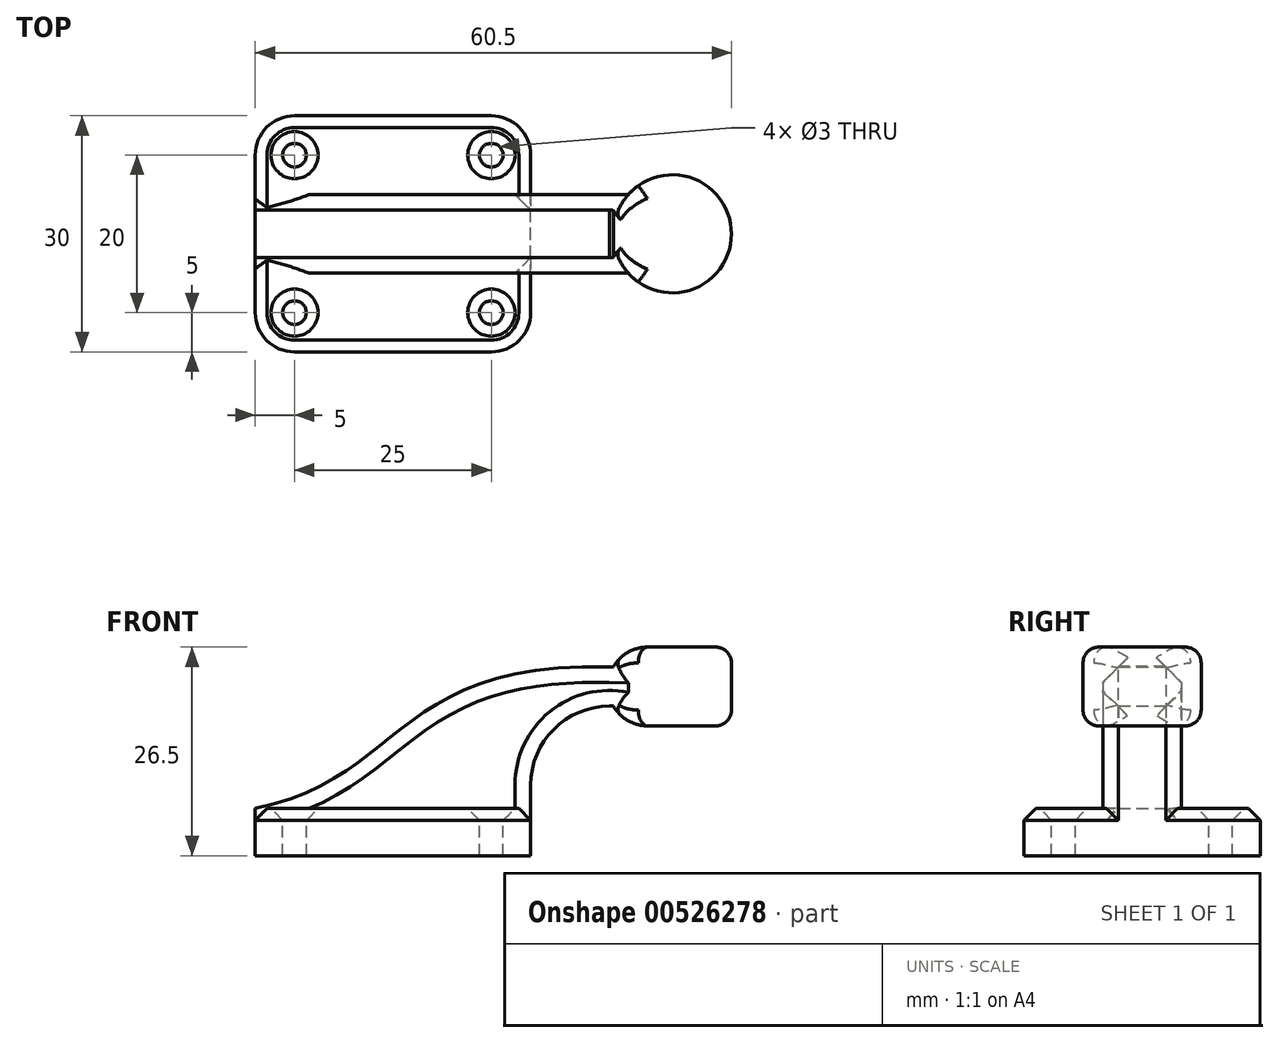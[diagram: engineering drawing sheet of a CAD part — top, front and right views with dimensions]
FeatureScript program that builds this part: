
annotation { "Feature Type Name" : "Feature", "Feature Type Description" : "" }
export const myFeature = defineFeature(function(context is Context, id is Id, definition is map)
    precondition{}
    {
        {
            var Q0;
            Q0=qCreatedBy(makeId("Front.planeOp"),FACE);
            var sketch = newSketch(context, id + "F0", { "sketchPlane" : qUnion([Q0])});
            skLineSegment(sketch, "E0.bottom", {"start": v(17.5, -3) * mm, "end": v(-17.5, -3) * mm});
            skLineSegment(sketch, "E0.top", {"start": v(17.5, 3) * mm, "end": v(-17.5, 3) * mm});
            skLineSegment(sketch, "E0.left", {"start": v(17.5, -3) * mm, "end": v(17.5, 3) * mm});
            skLineSegment(sketch, "E0.right", {"start": v(-17.5, -3) * mm, "end": v(-17.5, 3) * mm});
            skPoint(sketch, "E0.middle", {"position": v(0, 0) * mm});
            skLineSegment(sketch, "E1", {"start": v(17.5, 3) * mm, "end": v(17.5, 6) * mm});
            skArc(sketch, "E2", {"start": v(17.5, 6) * mm, "mid": v(20.43, 13.07) * mm, "end": v(27.5, 16) * mm});
            skLineSegment(sketch, "E3", {"start": v(27.5, 16) * mm, "end": v(35.5, 16) * mm});
            skLineSegment(sketch, "E4.bottom", {"start": v(43, 13.5) * mm, "end": v(28, 13.5) * mm});
            skLineSegment(sketch, "E4.top", {"start": v(43, 23.5) * mm, "end": v(28, 23.5) * mm});
            skLineSegment(sketch, "E4.left", {"start": v(43, 13.5) * mm, "end": v(43, 23.5) * mm});
            skLineSegment(sketch, "E4.right", {"start": v(28, 13.5) * mm, "end": v(28, 23.5) * mm});
            skPoint(sketch, "E4.middle", {"position": v(35.5, 18.5) * mm});
            skLineSegment(sketch, "E5", {"start": v(35.5, 13.5) * mm, "end": v(35.5, 18.5) * mm});
            skLineSegment(sketch, "E6", {"start": v(35.5, 18.5) * mm, "end": v(35.5, 23.5) * mm});
            skLineSegment(sketch, "E7.0", {"start": v(27.5, 21) * mm, "end": v(35.5, 21) * mm});
            skArc(sketch, "E7.1", {"start": v(12.5, 6) * mm, "mid": v(16.9, 16.6) * mm, "end": v(27.5, 21) * mm});
            skLineSegment(sketch, "E7.2", {"start": v(12.5, 5.23) * mm, "end": v(12.5, 6) * mm});
            skFitSpline(sketch, "E8", {"points": [v(-17.5, 3) * mm, v(27.5, 21) * mm], "startDerivative": vector(56.72, 11.59) * mm, "endDerivative": vector(82.5, -1.9) * mm});
            skSolve(sketch);
        }
        {
            var Q0;
            Q0=makeQuery(id+"F0.imprint","IMPRINT",FACE,{"disambiguationData":[TD([[makeQuery(id+"F0.imprint","IMPRINT",EDGE,{"derivedFrom":sQuery(id+"F0.wireOp",EDGE,"E0.bottom")}),-1.0]])]});
            extrude(context, id + "F1", {"entities" : qUnion([Q0]), "endBound" : BoundingType.SYMMETRIC, "depth" : 30 * mm, "offsetDistance" : 25 * mm});
        }
        {
            var Q0;
            Q0=makeQuery(id+"F0.imprint","IMPRINT",FACE,{"disambiguationData":[TD([[makeQuery(id+"F0.imprint","IMPRINT",EDGE,{"derivedFrom":sQuery(id+"F0.wireOp",EDGE,"E0.top")}),-1.0]])]});
            extrude(context, id + "F2", {"entities" : qUnion([Q0]), "operationType" : NewBodyOperationType.ADD, "endBound" : BoundingType.SYMMETRIC, "depth" : 10 * mm, "offsetDistance" : 25 * mm});
        }
        {
            var Q0;
            {var subQ0=sQuery(id+"F0.wireOp",EDGE,"E4.right");var subQ1=sQuery(id+"F0.wireOp",EDGE,"E4.top");var subQ2=makeQuery(id+"F0.imprint","INTERSECT",VERTEX,{"derivedFrom":[subQ1,subQ0]});Q0=makeQuery(id+"F0.imprint","IMPRINT",FACE,{"disambiguationData":[TD([[makeQuery(id+"F0.imprint","IMPRINT",EDGE,{"disambiguationData":[TD([[subQ2,1.0]])],"derivedFrom":subQ1}),1.0]])]});}
            var Q1;
            {var subQ1=sQuery(id+"F0.wireOp",EDGE,"E5");var subQ5=sQuery(id+"F0.wireOp",EDGE,"E3");var subQ6=makeQuery(id+"F0.imprint","INTERSECT",VERTEX,{"derivedFrom":[subQ5,subQ1]});Q1=makeQuery(id+"F0.imprint","IMPRINT",FACE,{"disambiguationData":[TD([[makeQuery(id+"F0.imprint","IMPRINT",EDGE,{"disambiguationData":[TD([[subQ6,1.0]])],"derivedFrom":subQ5}),1.0]])]});}
            var Q2;
            {var subQ0=sQuery(id+"F0.wireOp",EDGE,"E5");var subQ1=sQuery(id+"F0.wireOp",EDGE,"E3");var subQ2=makeQuery(id+"F0.imprint","INTERSECT",VERTEX,{"derivedFrom":[subQ1,subQ0]});Q2=makeQuery(id+"F0.imprint","IMPRINT",FACE,{"disambiguationData":[TD([[makeQuery(id+"F0.imprint","IMPRINT",EDGE,{"disambiguationData":[TD([[subQ2,1.0]])],"derivedFrom":subQ1}),-1.0]])]});}
            extrude(context, id + "F3", {"entities" : qUnion([Q0, Q1, Q2]), "operationType" : NewBodyOperationType.ADD, "endBound" : BoundingType.SYMMETRIC, "depth" : 10 * mm, "offsetDistance" : 25 * mm});
        }
        {
            var Q0;
            {var subQ4=sQuery(id+"F0.wireOp",EDGE,"E4.left");Q0=makeQuery(id+"F0.imprint","IMPRINT",FACE,{"disambiguationData":[TD([[makeQuery(id+"F0.imprint","IMPRINT",EDGE,{"derivedFrom":subQ4}),1.0]])]});}
            var Q1;
            Q1=sQuery(id+"F0.wireOp",EDGE,"E6");
            revolve(context, id + "F4", {"operationType" : NewBodyOperationType.ADD, "entities" : qUnion([Q0]), "axis" : qUnion([Q1]), "revolveType" : RevolveType.FULL});
        }
        {
            var Q0;
            Q0=makeQuery(id+"F1.opExtrude","CAP_EDGE",EDGE,{"disambiguationData":[OSD([sQuery(id+"F0.wireOp",EDGE,"E0.right")])],"isStart":false});
            var Q1;
            Q1=makeQuery(id+"F1.opExtrude","CAP_EDGE",EDGE,{"disambiguationData":[OSD([sQuery(id+"F0.wireOp",EDGE,"E0.left")])],"isStart":false});
            var Q2;
            Q2=makeQuery(id+"F1.opExtrude","CAP_EDGE",EDGE,{"disambiguationData":[OSD([sQuery(id+"F0.wireOp",EDGE,"E0.left")])],"isStart":true});
            var Q3;
            Q3=makeQuery(id+"F1.opExtrude","CAP_EDGE",EDGE,{"disambiguationData":[OSD([sQuery(id+"F0.wireOp",EDGE,"E0.right")])],"isStart":true});
            var Q4;
            Q4=makeQuery(id+"F3.opExtrude","SWEPT_EDGE",EDGE,{"disambiguationData":[OSD([sQuery(id+"F0.wireOp",EDGE,"E4.top"),sQuery(id+"F0.wireOp",EDGE,"E4.right")])]});
            var Q5;
            Q5=makeQuery(id+"F3.opExtrude","SWEPT_EDGE",EDGE,{"disambiguationData":[OSD([sQuery(id+"F0.wireOp",EDGE,"E4.bottom"),sQuery(id+"F0.wireOp",EDGE,"E4.right")])]});
            fillet(context, id + "F5", {"entities" : qUnion([Q0, Q1, Q2, Q3, Q4, Q5]), "radius" : 5 * mm, "tangentPropagation" : true, "allowEdgeOverflow" : false});
        }
        {
            var Q0;
            Q0=makeQuery(id+"F2.opExtrude","CAP_EDGE",EDGE,{"disambiguationData":[OSD([sQuery(id+"F0.wireOp",EDGE,"E8")])],"isStart":true});
            var Q1;
            Q1=makeQuery(id+"F2.opExtrude","CAP_EDGE",EDGE,{"disambiguationData":[OSD([sQuery(id+"F0.wireOp",EDGE,"E8")])],"isStart":false});
            var Q2;
            Q2=makeQuery(id+"F2.opExtrude","SWEPT_FACE",FACE,{"disambiguationData":[OSD([sQuery(id+"F0.wireOp",EDGE,"E2")])]});
            chamfer(context, id + "F6", {"entities" : qUnion([Q0, Q1, Q2]), "width" : 2 * mm, "tangentPropagation" : true});
        }
        {
            var Q0;
            Q0=makeQuery(id+"F1.opExtrude","CAP_EDGE",EDGE,{"disambiguationData":[OSD([sQuery(id+"F0.wireOp",EDGE,"E0.top")])],"isStart":true});
            var Q1;
            Q1=makeQuery(id+"F1.opExtrude","CAP_EDGE",EDGE,{"disambiguationData":[OSD([sQuery(id+"F0.wireOp",EDGE,"E0.top")])],"isStart":false});
            chamfer(context, id + "F7", {"entities" : qUnion([Q0, Q1]), "width" : 1.5 * mm, "tangentPropagation" : true});
        }
        {
            var Q0;
            Q0=makeQuery(id+"F4.opRevolve","SWEPT_EDGE",EDGE,{"disambiguationData":[OSD([sQuery(id+"F0.wireOp",EDGE,"E4.top"),sQuery(id+"F0.wireOp",EDGE,"E4.left")])]});
            var Q1;
            Q1=makeQuery(id+"F4.opRevolve","SWEPT_EDGE",EDGE,{"disambiguationData":[OSD([sQuery(id+"F0.wireOp",EDGE,"E4.bottom"),sQuery(id+"F0.wireOp",EDGE,"E4.left")])]});
            fillet(context, id + "F8", {"entities" : qUnion([Q0, Q1]), "radius" : 2 * mm, "tangentPropagation" : true, "allowEdgeOverflow" : false});
        }
        {
            var Q0;
            {var subQ2=sQuery(id+"F0.wireOp",EDGE,"E0.top");var subQ3=sQuery(id+"F0.wireOp",EDGE,"E0.right");var subQ4=sQuery(id+"F0.wireOp",EDGE,"E0.left");Q0=makeQuery(id+"F2.boolean.opBoolean","SPLIT",FACE,{"disambiguationData":[TD([makeQuery(id+"F1.opExtrude","CAP_FACE",FACE,{"disambiguationData":[OSD([sQuery(id+"F0.wireOp",EDGE,"E0.bottom"),subQ2,subQ4,subQ3])],"isStart":true})])],"derivedFrom":makeQuery(id+"F1.opExtrude","SWEPT_FACE",FACE,{"disambiguationData":[OSD([subQ2])]})});}
            var sketch = newSketch(context, id + "F9", { "sketchPlane" : qUnion([Q0])});
            skPoint(sketch, "E9", {"position": v(-12.5, 10) * mm});
            skPoint(sketch, "E10", {"position": v(12.5, 10) * mm});
            skSolve(sketch);
        }
        {
            var Q0;
            {var subQ2=sQuery(id+"F0.wireOp",EDGE,"E0.top");var subQ3=sQuery(id+"F0.wireOp",EDGE,"E0.right");var subQ4=sQuery(id+"F0.wireOp",EDGE,"E0.left");Q0=makeQuery(id+"F2.boolean.opBoolean","SPLIT",FACE,{"disambiguationData":[TD([makeQuery(id+"F1.opExtrude","CAP_FACE",FACE,{"disambiguationData":[OSD([sQuery(id+"F0.wireOp",EDGE,"E0.bottom"),subQ2,subQ4,subQ3])],"isStart":false})])],"derivedFrom":makeQuery(id+"F1.opExtrude","SWEPT_FACE",FACE,{"disambiguationData":[OSD([subQ2])]})});}
            var sketch = newSketch(context, id + "F10", { "sketchPlane" : qUnion([Q0])});
            skPoint(sketch, "E11", {"position": v(12.5, -10) * mm});
            skPoint(sketch, "E12", {"position": v(-12.5, -10) * mm});
            skSolve(sketch);
        }
        {
            var Q0;
            Q0=sQuery(id+"F9.wireOp",VERTEX,"E10");
            var Q1;
            Q1=sQuery(id+"F9.wireOp",VERTEX,"E9");
            var Q2;
            Q2=sQuery(id+"F10.wireOp",VERTEX,"E12");
            var Q3;
            Q3=sQuery(id+"F10.wireOp",VERTEX,"E11");
            var Q4;
            Q4=makeQuery(id+"F1.opExtrude","SWEPT_BODY",BODY,{"disambiguationData":[OSD([sQuery(id+"F0.wireOp",EDGE,"E0.bottom"),sQuery(id+"F0.wireOp",EDGE,"E0.top"),sQuery(id+"F0.wireOp",EDGE,"E0.left"),sQuery(id+"F0.wireOp",EDGE,"E0.right")])]});
            hole(context, id + "F11", {"style" : HoleStyle.C_SINK, "endStyle" : HoleEndStyle.BLIND, "holeDiameter" : 3 * mm, "cSinkDiameter" : 6 * mm, "cSinkAngle" : 90 * degree, "holeDepth" : 10 * mm, "isTappedThrough" : true, "tappedDepth" : 12 * mm, "tapClearance" : 3, "locations" : qUnion([Q0, Q1, Q2, Q3]), "scope" : qUnion([Q4])});
        }
    });
